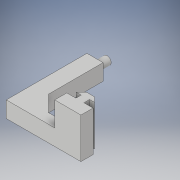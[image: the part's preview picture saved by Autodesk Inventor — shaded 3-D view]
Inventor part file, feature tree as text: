
AUTODESK INVENTOR PART (.ipt)
format: ipt  version: 2018 (Build 220112000, 112)  size: 155,136 bytes
history: native  units: in
note: dims shown in document units (in); Inventor stores cm internally (conversion verified against a paired STEP export)
features: sketch x6, extrude x5, hole x1, chamfer x1
ambient origin geometry x8: Origin, YZ Plane, XZ Plane, XY Plane, X Axis, Y Axis, Z Axis, Center Point
bodies: Solid1 (feature_tree)
feature tree (13):
  extrude  "Extrusion1"  Depth=0.3in
  extrude  "Extrusion2"  Depth=0.26in
  extrude  "Extrusion3"  Depth=0.12in
  extrude  "Extrusion4"  Depth=0.12in
  hole  "Hole1"  [1 undecoded]
  extrude  "Extrusion5"  Depth=1.2in TaperAngle=0.0deg
  chamfer  "Chamfer1"  Distance=0.4in
  sketch  "Sketch1"  dims[d0=0.65in d1=0.3in]
  sketch  "Sketch3"  dims[d2=0.225in d3=0.26in]
  sketch  "Sketch4"  dims[d4=0.2in d5=0.12in]
  sketch  "Sketch5"  dims[d6=0.12in d7=0.12in]
  sketch  "Sketch6"  dims[d8=1.0in d9=0.0in d10=0.25in]
  sketch  "Sketch7"  dims[d11=0.4in d12=1.2in d13=0.0in d14=0.4in d15=0.4in d16=1.75in d17=0.0in d18=0.2in d19=0.2in d20=0.3in d21=0.0in d22=0.11in d23=0.75in d24=0.375in d25=0.25in d26=0.5635in d27=0.63in d28=0.8108in d29=0.4in d30=0.4in d31=0.0in d32=0.4in d33=0.125in d34=45.0deg]
note: 1 required parameter value undecoded (feature->parameter linkage not recoverable at this tier; creation-order binding heuristic only, values carry confidence <= 0.55)
